# Revit family: 94534002
name_source: partatom
category: Modelos genéricos
revit_build: Autodesk Revit 2016 (Build: 20150220_1215(x64)
units: mm (PartAtom-declared; Revit-internal decimal feet)

## family parameters
Com base no plano de trabalho = Não
Compartilhado = Não
Corte com vazios quando carregados = Não
Cota do conector redondo = Utilizar diâmetro
Pode hospedar o vergalhão = Não
Ponto de cálculo do ambiente = Não
Sempre na vertical = Sim
Tipo de parte = Normal

## types (1)
- Calha Umida Tramontina - 94534002- 90-CM
    Código de montagem = Calha Umida Tramontina - 94534002- 90-CM
    Descrição = Tramontina Cubas Quadrum 50 - 94007-103
    Desenvolvedor = Factory Cursos
    Diametro do cano de saida = 40  [stored 0.131234 ft]
    Fabricante = Tramontina
    Manual de Instalação = <Nenhum>
    Modelo = Calha Umida Tramontina - 94534002- 90-CM
    Site do desenvolvedor = www.factorycursos.com.br
    Tamanho (mm) = 900 X 185
    Tipo de imagem = <Nenhum>
    URL = www.tramontina.com.br

note: [stored X ft] marks values corroborated as IEEE doubles in the binary element streams (Revit-internal decimal feet)
